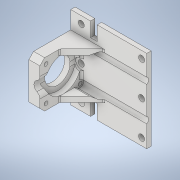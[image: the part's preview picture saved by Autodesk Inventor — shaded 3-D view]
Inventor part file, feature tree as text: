
AUTODESK INVENTOR PART (.ipt)
format: ipt  version: 2020 (Build 240168000, 168)  size: 632,832 bytes
history: native  units: mm
features: sketch x28, extrude x27, chamfer x7, other x5, pattern_linear x5, mirror x3, fillet x2
ambient origin geometry x8: Origin, YZ Plane, XZ Plane, XY Plane, X Axis, Y Axis, Z Axis, Center Point
bodies: Body1 (feature_tree), Body2 (feature_tree), Body3 (feature_tree)
feature tree (77):
  other  "Bryła1"
  extrude  "Wyciągnięcie proste1"  Depth=74.0mm
  extrude  "Wyciągnięcie proste2"  Depth=74.0mm
  extrude  "Wyciągnięcie proste3"  Depth=25.0mm TaperAngle=0.0deg
  extrude  "Wyciągnięcie proste4"  Depth=20.0mm
  other  "Płaszczyzna konstrukcyjna1"
  extrude  "Wyciągnięcie proste5"  Depth=20.0mm
  pattern_linear  "Szyk prostokątny1"  Spacing1=11.0mm  [1 undecoded]
  chamfer  "Faza1"  Distance=11.0mm
  chamfer  "Faza2"  Distance=19.8mm
  chamfer  "Faza3"  Distance=2.05mm
  extrude  "Wyciągnięcie proste6"  Depth=7.9mm
  extrude  "Wyciągnięcie proste7"  TaperAngle=0.0deg  [1 undecoded]
  extrude  "Wyciągnięcie proste8"  TaperAngle=0.0deg  [1 undecoded]
  extrude  "Wyciągnięcie proste9"  Depth=2.05mm
  extrude  "Wyciągnięcie proste10"  Depth=7.9mm
  extrude  "Wyciągnięcie proste11"  TaperAngle=0.0deg  [1 undecoded]
  pattern_linear  "Szyk prostokątny2"  Spacing1=0.0mm  [1 undecoded]
  extrude  "Wyciągnięcie proste12"  Depth=1.9mm TaperAngle=0.0deg
  other  "Płaszczyzna konstrukcyjna2"
  mirror  "Odbij1"
  chamfer  "Faza4"  Distance=4.0mm
  extrude  "Wyciągnięcie proste13"  Depth=5.5mm
  pattern_linear  "Szyk prostokątny3"  Spacing1=5.5mm  [1 undecoded]
  extrude  "Wyciągnięcie proste14"  Depth=6.0mm
  pattern_linear  "Szyk prostokątny4"  Spacing1=6.0mm  [1 undecoded]
  extrude  "Wyciągnięcie proste15"  Depth=54.78mm
  pattern_linear  "Szyk prostokątny5"  Spacing1=-37.0mm  [1 undecoded]
  extrude  "Wyciągnięcie proste16"  Depth=27.39mm
  other  "Płaszczyzna konstrukcyjna3"
  mirror  "Odbij2"
  extrude  "Wyciągnięcie proste17"  Depth=50.0mm TaperAngle=0.0deg
  extrude  "Wyciągnięcie proste18"  Depth=30.0mm
  extrude  "Wyciągnięcie proste19"  Depth=2.0mm TaperAngle=45.0deg
  extrude  "Wyciągnięcie proste20"  Depth=2.0mm TaperAngle=45.0deg
  extrude  "Wyciągnięcie proste21"  Depth=2.0mm TaperAngle=45.0deg
  chamfer  "Faza5"  Distance=22.9mm
  extrude  "Wyciągnięcie proste23"  Depth=12.0mm
  extrude  "Wyciągnięcie proste25"  Depth=12.0mm
  sketch  "Szkic28"
  extrude  "Wyciągnięcie proste26"  Depth=100.0mm
  extrude  "Wyciągnięcie proste24"  Depth=13.0mm
  extrude  "Wyciągnięcie proste27"  Depth=13.0mm
  chamfer  "Faza6"  Distance=25.0mm
  fillet  "Zaokrąglenie1"  Radius=25.0mm
  extrude  "Wyciągnięcie proste28"  Depth=25.0mm
  fillet  "Zaokrąglenie2"  Radius=55.0mm
  other  "Płaszczyzna konstrukcyjna5"
  mirror  "Odbij4"
  chamfer  "Faza7"  [1 undecoded]
  sketch  "Szkic1"
  sketch  "Szkic2"
  sketch  "Szkic3"
  sketch  "Szkic4"
  sketch  "Szkic5"
  sketch  "Szkic6"
  sketch  "Szkic7"
  sketch  "Szkic8"
  sketch  "Szkic9"
  sketch  "Szkic10"
  sketch  "Szkic12"
  sketch  "Szkic13"
  sketch  "Szkic15"
  sketch  "Szkic16"
  sketch  "Szkic17"
  sketch  "Szkic18"
  sketch  "Szkic19"
  sketch  "Szkic20"
  sketch  "Szkic21"
  sketch  "Szkic22"
  sketch  "Szkic23"
  sketch  "Szkic25"
  sketch  "Szkic26"
  sketch  "Szkic27"
  sketch  "Szkic29"
  sketch  "Szkic30"
  sketch  "Szkic31"
note: 9 required parameter values undecoded (feature->parameter linkage not recoverable at this tier; creation-order binding heuristic only, values carry confidence <= 0.55)
